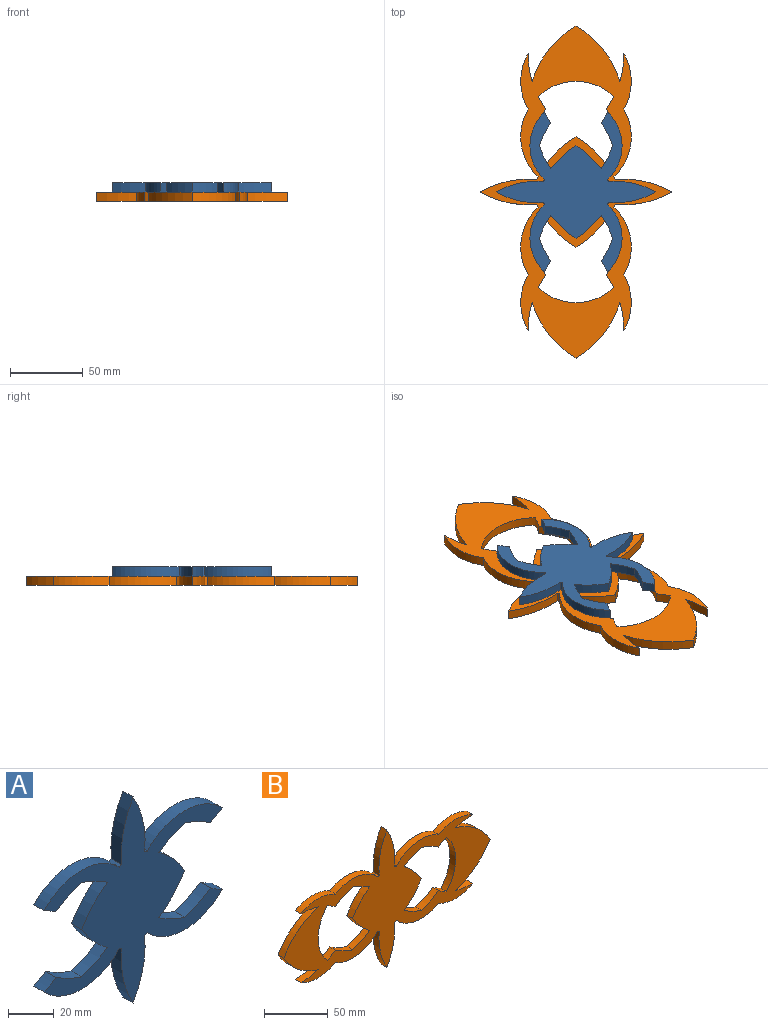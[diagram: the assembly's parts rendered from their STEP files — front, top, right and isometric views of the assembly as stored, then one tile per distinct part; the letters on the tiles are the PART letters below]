
ASSEMBLY  parts=2 mates=1
PART A: 30 faces, bbox 109.8x6.4x110 mm
  f0: cylinder r=54.99mm len=17.41mm, axis (0,1,0), area 150.8mm2, adj f1,f27,f28,f29
  f1: cylinder r=54.99mm len=17.41mm, axis (0,1,0), area 150.8mm2, adj f0,f2,f28,f29
  f2: cylinder r=54.99mm len=15.88mm, axis (0,1,0), area 112.7mm2, adj f1,f3,f28,f29
  f3: cylinder r=54.99mm len=15.88mm, axis (0,1,0), area 112.7mm2, adj f2,f4,f28,f29
  f4: cylinder r=54.99mm len=7.26mm, axis (0,1,0), area 53.8mm2, adj f3,f5,f28,f29
  f5: cylinder r=31.75mm len=46.27mm, axis (0,1,0), area 329.2mm2, adj f4,f6,f28,f29
  f6: cylinder r=54.99mm len=6.35mm, axis (0,1,0), area 10.4mm2, adj f5,f7,f28,f29
  f7: cylinder r=54.99mm len=32.54mm, axis (0,1,0), area 214.9mm2, adj f6,f8,f28,f29
  f8: cylinder r=54.99mm len=32.54mm, axis (0,1,0), area 214.9mm2, adj f7,f9,f28,f29
  f9: cylinder r=54.99mm len=6.35mm, axis (0,1,0), area 10.4mm2, adj f8,f10,f28,f29
  f10: cylinder r=31.75mm len=46.27mm, axis (0,1,0), area 329.2mm2, adj f9,f11,f28,f29
  f11: cylinder r=54.99mm len=7.26mm, axis (0,1,0), area 53.8mm2, adj f10,f12,f28,f29
  f12: cylinder r=54.99mm len=15.88mm, axis (0,1,0), area 112.7mm2, adj f11,f13,f28,f29
  f13: cylinder r=54.99mm len=15.88mm, axis (0,1,0), area 112.7mm2, adj f12,f14,f28,f29
  f14: cylinder r=54.99mm len=17.41mm, axis (0,1,0), area 150.8mm2, adj f13,f15,f28,f29
  f15: cylinder r=54.99mm len=17.41mm, axis (0,1,0), area 150.8mm2, adj f14,f16,f28,f29
  f16: cylinder r=54.99mm len=15.88mm, axis (0,1,0), area 112.7mm2, adj f15,f17,f28,f29
  f17: cylinder r=54.99mm len=15.88mm, axis (0,1,0), area 112.7mm2, adj f16,f18,f28,f29
  f18: cylinder r=54.99mm len=7.26mm, axis (0,1,0), area 53.8mm2, adj f17,f19,f28,f29
  f19: cylinder r=31.75mm len=46.27mm, axis (0,1,0), area 329.2mm2, adj f18,f20,f28,f29
  f20: cylinder r=54.99mm len=6.35mm, axis (0,1,0), area 10.4mm2, adj f19,f21,f28,f29
  f21: cylinder r=54.99mm len=32.54mm, axis (0,1,0), area 214.9mm2, adj f20,f22,f28,f29
  f22: cylinder r=54.99mm len=32.54mm, axis (0,1,0), area 214.9mm2, adj f21,f23,f28,f29
  f23: cylinder r=54.99mm len=6.35mm, axis (0,1,0), area 10.4mm2, adj f22,f24,f28,f29
  f24: cylinder r=31.75mm len=46.27mm, axis (0,1,0), area 329.2mm2, adj f23,f25,f28,f29
  f25: cylinder r=54.99mm len=7.26mm, axis (0,1,0), area 53.8mm2, adj f24,f26,f28,f29
  f26: cylinder r=54.99mm len=15.88mm, axis (0,1,0), area 112.7mm2, adj f25,f27,f28,f29
  f27: cylinder r=54.99mm len=15.88mm, axis (0,1,0), area 112.7mm2, adj f0,f26,f28,f29
  f28: plane 109.99x109.77mm, normal (0,-1,0), area 4061.6mm2, adj f0,f1,f2,f3,f4,f5,f6,f7
  f29: plane 109.99x109.77mm, normal (0,1,0), area 4061.6mm2, adj f0,f1,f2,f3,f4,f5,f6,f7
PART B: 44 faces, bbox 228.6x6.4x132 mm
  f0: cylinder r=65.99mm len=6.35mm, axis (0,1,0), area 12.5mm2, adj f1,f41,f42,f43
  f1: cylinder r=38.1mm len=46.81mm, axis (0,1,0), area 324.2mm2, adj f0,f2,f42,f43
  f2: cylinder r=38.1mm len=38.1mm, axis (0,1,0), area 253.4mm2, adj f1,f3,f42,f43
  f3: cylinder r=65.99mm len=19.05mm, axis (0,1,0), area 122.7mm2, adj f2,f4,f42,f43
  f4: cylinder r=65.99mm len=38.1mm, axis (0,1,0), area 316.1mm2, adj f3,f5,f42,f43
  f5: cylinder r=65.99mm len=38.1mm, axis (0,1,0), area 316.1mm2, adj f4,f6,f42,f43
  f6: cylinder r=65.99mm len=19.05mm, axis (0,1,0), area 122.7mm2, adj f5,f7,f42,f43
  f7: cylinder r=38.1mm len=38.1mm, axis (0,1,0), area 253.4mm2, adj f6,f8,f42,f43
  f8: cylinder r=38.1mm len=46.81mm, axis (0,1,0), area 324.2mm2, adj f7,f9,f42,f43
  f9: cylinder r=65.99mm len=6.35mm, axis (0,1,0), area 12.5mm2, adj f8,f10,f42,f43
  f10: cylinder r=65.99mm len=39.05mm, axis (0,1,0), area 257.9mm2, adj f9,f11,f42,f43
  f11: cylinder r=65.99mm len=39.05mm, axis (0,1,0), area 257.9mm2, adj f10,f12,f42,f43
  f12: cylinder r=65.99mm len=6.35mm, axis (0,1,0), area 12.5mm2, adj f11,f13,f42,f43
  f13: cylinder r=38.1mm len=46.81mm, axis (0,1,0), area 324.2mm2, adj f12,f14,f42,f43
  f14: cylinder r=38.1mm len=38.1mm, axis (0,1,0), area 253.4mm2, adj f13,f15,f42,f43
  f15: cylinder r=65.99mm len=19.05mm, axis (0,1,0), area 122.7mm2, adj f14,f16,f42,f43
  f16: cylinder r=65.99mm len=38.1mm, axis (0,1,0), area 316.1mm2, adj f15,f17,f42,f43
  f17: cylinder r=65.99mm len=38.1mm, axis (0,1,0), area 316.1mm2, adj f16,f18,f42,f43
  f18: cylinder r=65.99mm len=19.05mm, axis (0,1,0), area 122.7mm2, adj f17,f19,f42,f43
  f19: cylinder r=38.1mm len=38.1mm, axis (0,1,0), area 253.4mm2, adj f18,f20,f42,f43
  f20: cylinder r=38.1mm len=46.81mm, axis (0,1,0), area 324.2mm2, adj f19,f21,f42,f43
  f21: cylinder r=65.99mm len=6.35mm, axis (0,1,0), area 12.5mm2, adj f20,f22,f42,f43
  f22: cylinder r=65.99mm len=39.05mm, axis (0,1,0), area 257.9mm2, adj f21,f41,f42,f43
  f23: cylinder r=65.99mm len=20.89mm, axis (0,1,0), area 180.9mm2, adj f24,f39,f42,f43
  f24: cylinder r=65.99mm len=19.05mm, axis (0,1,0), area 135.2mm2, adj f23,f25,f42,f43
  f25: cylinder r=65.99mm len=19.05mm, axis (0,1,0), area 135.2mm2, adj f24,f26,f42,f43
  f26: cylinder r=65.99mm len=8.71mm, axis (0,1,0), area 64.5mm2, adj f25,f27,f42,f43
  f27: cylinder r=38.1mm len=52.18mm, axis (0,1,0), area 365mm2, adj f26,f28,f42,f43
  f28: cylinder r=65.99mm len=8.71mm, axis (0,1,0), area 64.5mm2, adj f27,f29,f42,f43
  f29: cylinder r=65.99mm len=19.05mm, axis (0,1,0), area 135.2mm2, adj f28,f30,f42,f43
  f30: cylinder r=65.99mm len=19.05mm, axis (0,1,0), area 135.2mm2, adj f29,f39,f42,f43
  f31: cylinder r=65.99mm len=20.89mm, axis (0,1,0), area 180.9mm2, adj f32,f40,f42,f43
  f32: cylinder r=65.99mm len=20.89mm, axis (0,1,0), area 180.9mm2, adj f31,f33,f42,f43
  f33: cylinder r=65.99mm len=19.05mm, axis (0,1,0), area 135.2mm2, adj f32,f34,f42,f43
  f34: cylinder r=65.99mm len=19.05mm, axis (0,1,0), area 135.2mm2, adj f33,f35,f42,f43
  f35: cylinder r=65.99mm len=8.71mm, axis (0,1,0), area 64.5mm2, adj f34,f36,f42,f43
  f36: cylinder r=38.1mm len=52.18mm, axis (0,1,0), area 365mm2, adj f35,f37,f42,f43
  f37: cylinder r=65.99mm len=8.71mm, axis (0,1,0), area 64.5mm2, adj f36,f38,f42,f43
  f38: cylinder r=65.99mm len=19.05mm, axis (0,1,0), area 135.2mm2, adj f37,f40,f42,f43
  f39: cylinder r=65.99mm len=20.89mm, axis (0,1,0), area 180.9mm2, adj f23,f30,f42,f43
  f40: cylinder r=65.99mm len=19.05mm, axis (0,1,0), area 135.2mm2, adj f31,f38,f42,f43
  f41: cylinder r=65.99mm len=39.05mm, axis (0,1,0), area 257.9mm2, adj f0,f22,f42,f43
  f42: plane 228.6x131.98mm, normal (0,-1,0), area 10082.4mm2, adj f0,f1,f2,f3,f4,f5,f6,f7
  f43: plane 228.6x131.98mm, normal (0,1,0), area 10082.4mm2, adj f0,f1,f2,f3,f4,f5,f6,f7
PLACE A rot(axis=(-0.58,-0.58,0.58),120deg) t=(0,0,0)mm
PLACE B rot(axis=(0.58,0.58,0.58),120deg) t=(0,0,0)mm
MATE fastened A.f29 <-> B.f43  axis (0,0,-1) through (0,0,0)mm
